# Revit family: Receptacle_Straight-Blade_Leviton_Decora-Duplex
name_source: partatom
category: Electrical Fixtures
units: mm (PartAtom-declared; Revit-internal decimal feet)

## family parameters
Always vertical = No
Cut with Voids When Loaded = No
Maintain Annotation Orientation = No
Part Type = Normal
Room Calculation Point = No
Round Connector Dimension = Use Diameter
Shared = No
Work Plane-Based = Yes

## types (1)
- Receptacle_Straight-Blade_Leviton_Decora-Duplex
    Acceptable Loads = as Specified
    Assembly Code = D5020100
    Backing Color = Thermoplastic - Leviton - Black
    Default Elevation = 4' - 0"
    Description = Leviton Product as Specified
    Expected Lifespan (Years) = 0
    Fixture Application = as Specified
    Fixture Grade = as Specified
    Fixture Height = 0' - 2 25/32"
    Fixture Material = Thermoplastic - Leviton - White
    Grounding = as Specified
    HP Rating = as Specified
    Installation Phase = Electrical Wiring
    Keynote = 16140
    MEP Amperage = 0 A
    MEP Apparent Power = 0 VA
    Maintenance Schedule (Months) = 0
    Manufacturer = Leviton Mfg. Co., Inc.
    Manufacturer Fax = 631-812-6252
    Manufacturer Website = http://www.leviton.com
    Maximum Amperage = 0
    Model = As Specified
    NEMA 5_15R 1 = Yes
    NEMA 5_15R 2 = Yes
    NEMA 5_20R 1 = No
    NEMA 5_20R 2 = No
    NEMA 6_15R 1 = No
    NEMA 6_15R 2 = No
    NEMA 6_20R 1 = No
    NEMA 6_20R 2 = No
    NEMA5-15Rvoidbot = 0' - 0 1/2"
    NEMA5-15Rvoidtop = 0' - 0 1/2"
    NEMA5-20Rvoidbot = 0' - 0 1/16"
    NEMA5-20Rvoidtop = 0' - 0 1/16"
    NEMA6-15Rvoidbot = 0' - 0 1/16"
    NEMA6-15Rvoidtop = 0' - 0 1/16"
    NEMA6-20Rvoidbot = 0' - 0 1/16"
    NEMA6-20Rvoidtop = 0' - 0 1/16"
    Number of Poles = 1
    Product Data = http://arcat.com
    Projection From Host = 0' - 0 1/4"
    Revision = R1_10-2012
    Sales Information = http://www.leviton.com
    Screw Mounts Location = 0' - 3 9/32"
    Send Message = http://www.arcat.com
    Standards Conformance = as Specified
    Termination = as Specified
    URL = http://www.leviton.com
    Unit Depth = 0' - 0 7/8"
    Unit Height = 0' - 4 1/16"
    Unit Width = 0' - 1 5/16"
    Voltage_MEP = 0 V
    Warranty Duration (Years) = 0

## geometry (parser evidence)
native form markers: Sweep x2
no freeform markers — native parametric forms only
